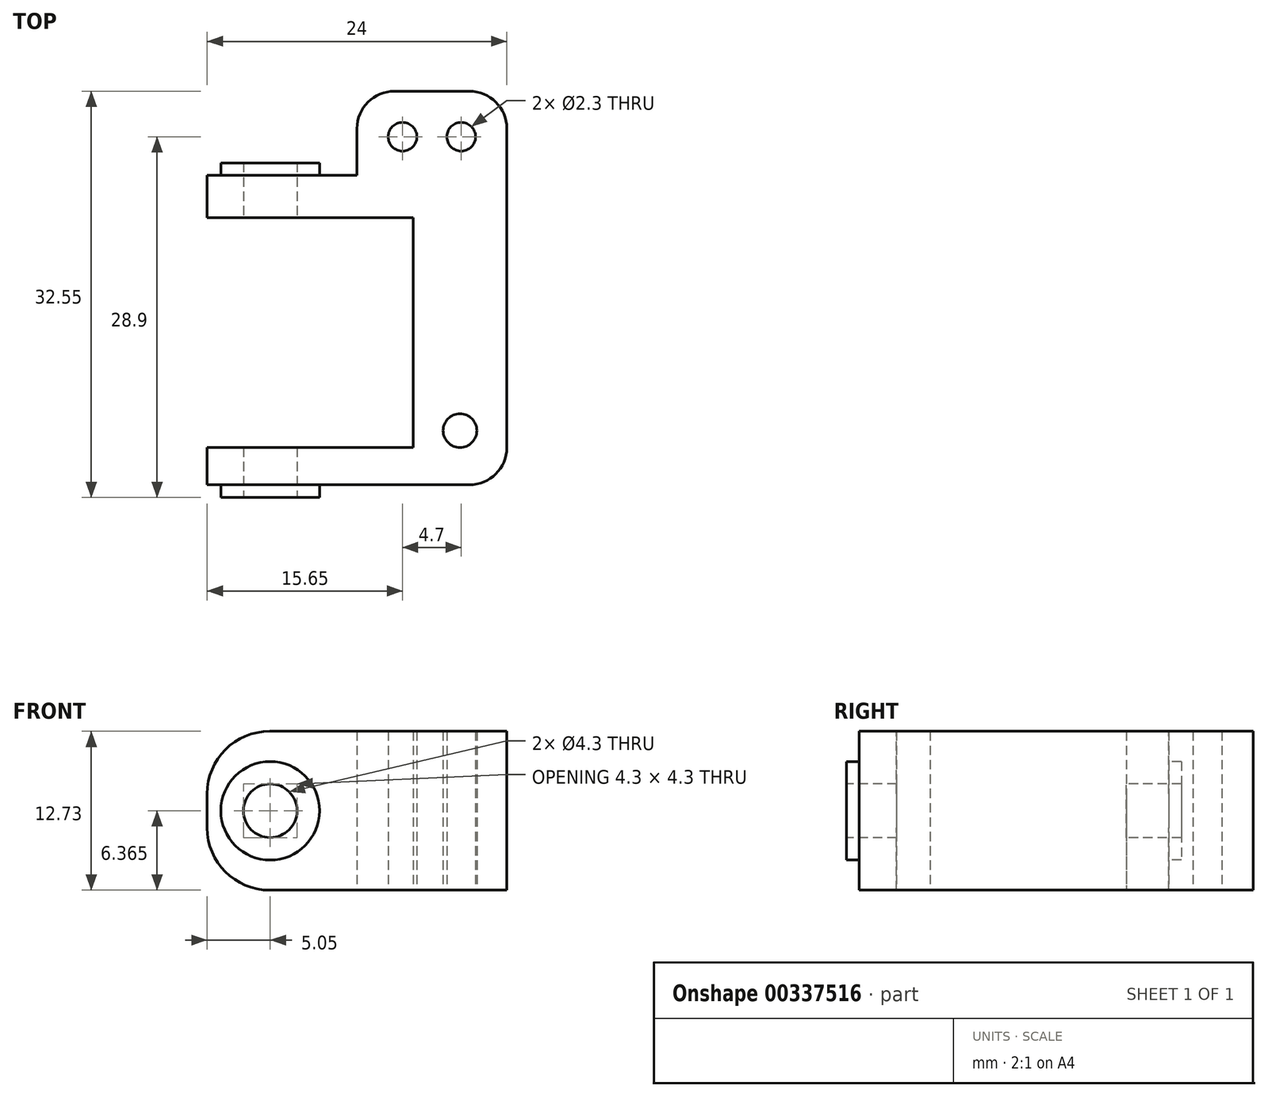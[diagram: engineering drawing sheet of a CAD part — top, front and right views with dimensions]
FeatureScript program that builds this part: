
annotation { "Feature Type Name" : "Feature", "Feature Type Description" : "" }
export const myFeature = defineFeature(function(context is Context, id is Id, definition is map)
    precondition{}
    {
        {
            var Q0;
            Q0=qCreatedBy(makeId("Top.planeOp"),FACE);
            var sketch = newSketch(context, id + "F0", { "sketchPlane" : qUnion([Q0])});
            skCircle(sketch, "E0", {"center": v(0, 0) * mm, "radius": 1.35 * mm});
            skLineSegment(sketch, "E1", {"start": v(1.35, 0) * mm, "end": v(3.75, 0) * mm, "construction": true});
            skLineSegment(sketch, "E2", {"start": v(3.75, 0) * mm, "end": v(3.75, -4.35) * mm});
            skLineSegment(sketch, "E3", {"start": v(3.75, -4.35) * mm, "end": v(-20.25, -4.35) * mm});
            skLineSegment(sketch, "E4", {"start": v(-20.25, -4.35) * mm, "end": v(-20.25, -1.35) * mm});
            skLineSegment(sketch, "E5", {"start": v(0, -1.35) * mm, "end": v(0, -4.35) * mm, "construction": true});
            skLineSegment(sketch, "E6", {"start": v(3.75, 0) * mm, "end": v(3.75, 27.2) * mm});
            skLineSegment(sketch, "E7", {"start": v(-20.25, -1.35) * mm, "end": v(-3.75, -1.35) * mm});
            skLineSegment(sketch, "E8", {"start": v(-3.75, -1.35) * mm, "end": v(-3.75, 17.05) * mm});
            skLineSegment(sketch, "E9", {"start": v(-1.35, 0) * mm, "end": v(-3.75, 0) * mm, "construction": true});
            skLineSegment(sketch, "E10", {"start": v(0, 1.35) * mm, "end": v(0, 4.35) * mm, "construction": true});
            skLineSegment(sketch, "E11", {"start": v(0, 4.35) * mm, "end": v(3.75, 4.35) * mm, "construction": true});
            skLineSegment(sketch, "E12", {"start": v(0, 4.35) * mm, "end": v(-3.75, 4.35) * mm, "construction": true});
            skLineSegment(sketch, "E13", {"start": v(3.75, 27.2) * mm, "end": v(-8.25, 27.2) * mm});
            skLineSegment(sketch, "E14", {"start": v(-8.25, 27.2) * mm, "end": v(-8.25, 20.45) * mm});
            skLineSegment(sketch, "E15", {"start": v(-8.25, 20.45) * mm, "end": v(3.75, 20.45) * mm, "construction": true});
            skLineSegment(sketch, "E16", {"start": v(-3.75, 17.05) * mm, "end": v(-3.75, 20.45) * mm});
            skLineSegment(sketch, "E17", {"start": v(-3.75, 17.05) * mm, "end": v(-20.25, 17.05) * mm});
            skLineSegment(sketch, "E18", {"start": v(-20.25, 17.05) * mm, "end": v(-20.25, 20.45) * mm});
            skLineSegment(sketch, "E19", {"start": v(-20.25, 20.45) * mm, "end": v(-8.25, 20.45) * mm});
            skCircle(sketch, "E20", {"center": v(0.1, 23.55) * mm, "radius": 1.15 * mm});
            skLineSegment(sketch, "E21", {"start": v(1.25, 23.55) * mm, "end": v(3.75, 23.55) * mm, "construction": true});
            skLineSegment(sketch, "E22", {"start": v(0.1, 24.7) * mm, "end": v(0.1, 27.2) * mm, "construction": true});
            skLineSegment(sketch, "E23", {"start": v(0.1, 23.55) * mm, "end": v(1.25, 23.55) * mm, "construction": true});
            skLineSegment(sketch, "E24", {"start": v(0.1, 23.55) * mm, "end": v(0.1, 24.7) * mm, "construction": true});
            skCircle(sketch, "E25", {"center": v(-4.6, 23.55) * mm, "radius": 1.15 * mm});
            skLineSegment(sketch, "E26", {"start": v(-4.6, 24.7) * mm, "end": v(-4.6, 27.2) * mm, "construction": true});
            skLineSegment(sketch, "E27", {"start": v(-5.75, 23.55) * mm, "end": v(-8.25, 23.55) * mm, "construction": true});
            skLineSegment(sketch, "E28", {"start": v(-4.6, 23.55) * mm, "end": v(-5.75, 23.55) * mm, "construction": true});
            skLineSegment(sketch, "E29", {"start": v(-4.6, 24.7) * mm, "end": v(-4.6, 23.55) * mm, "construction": true});
            skSolve(sketch);
        }
        {
            var Q0;
            Q0=makeQuery(id+"F0.imprint","IMPRINT",FACE,{"disambiguationData":[TD([[makeQuery(id+"F0.imprint","IMPRINT",EDGE,{"derivedFrom":sQuery(id+"F0.wireOp",EDGE,"E0")}),-1.0]])]});
            extrude(context, id + "F1", {"entities" : qUnion([Q0]), "depth" : 12.73 * mm});
        }
        {
            var Q0;
            Q0=makeQuery(id+"F1.opExtrude","SWEPT_FACE",FACE,{"disambiguationData":[OSD([sQuery(id+"F0.wireOp",EDGE,"E3")])]});
            var sketch = newSketch(context, id + "F2", { "sketchPlane" : qUnion([Q0])});
            skCircle(sketch, "E30", {"center": v(-15.2, 6.37) * mm, "radius": 2.15 * mm});
            skPoint(sketch, "E30.centerSnap0", {"position": v(-20.25, 6.37) * mm});
            skLineSegment(sketch, "E31", {"start": v(-20.25, 6.37) * mm, "end": v(-17.35, 6.37) * mm});
            skCircle(sketch, "E32", {"center": v(-15.2, 6.37) * mm, "radius": 3.95 * mm});
            skSolve(sketch);
        }
        {
            var Q0;
            Q0=makeQuery(id+"F2.imprint","IMPRINT",FACE,{"disambiguationData":[TD([[makeQuery(id+"F2.imprint","IMPRINT",EDGE,{"derivedFrom":sQuery(id+"F2.wireOp",EDGE,"E30")}),1.0]])]});
            extrude(context, id + "F3", {"entities" : qUnion([Q0]), "operationType" : NewBodyOperationType.REMOVE, "oppositeDirection" : true, "depth" : 25 * mm});
        }
        {
            var Q0;
            Q0=makeQuery(id+"F1.opExtrude","CAP_EDGE",EDGE,{"disambiguationData":[OSD([sQuery(id+"F0.wireOp",EDGE,"E4")])],"isStart":false});
            var Q1;
            Q1=makeQuery(id+"F1.opExtrude","CAP_EDGE",EDGE,{"disambiguationData":[OSD([sQuery(id+"F0.wireOp",EDGE,"E18")])],"isStart":false});
            var Q2;
            Q2=makeQuery(id+"F1.opExtrude","CAP_EDGE",EDGE,{"disambiguationData":[OSD([sQuery(id+"F0.wireOp",EDGE,"E4")])],"isStart":true});
            var Q3;
            Q3=makeQuery(id+"F1.opExtrude","CAP_EDGE",EDGE,{"disambiguationData":[OSD([sQuery(id+"F0.wireOp",EDGE,"E18")])],"isStart":true});
            fillet(context, id + "F4", {"entities" : qUnion([Q0, Q1, Q2, Q3]), "radius" : 5 * mm, "tangentPropagation" : true, "allowEdgeOverflow" : false});
        }
        {
            var Q0;
            Q0=makeQuery(id+"F1.opExtrude","SWEPT_EDGE",EDGE,{"disambiguationData":[OSD([sQuery(id+"F0.wireOp",EDGE,"E2"),sQuery(id+"F0.wireOp",EDGE,"E3")])]});
            fillet(context, id + "F5", {"entities" : qUnion([Q0]), "radius" : 3 * mm, "tangentPropagation" : true, "allowEdgeOverflow" : false});
        }
        {
            var Q0;
            Q0=makeQuery(id+"F1.opExtrude","SWEPT_EDGE",EDGE,{"disambiguationData":[OSD([sQuery(id+"F0.wireOp",EDGE,"E13"),sQuery(id+"F0.wireOp",EDGE,"E14")])]});
            var Q1;
            Q1=makeQuery(id+"F1.opExtrude","SWEPT_EDGE",EDGE,{"disambiguationData":[OSD([sQuery(id+"F0.wireOp",EDGE,"E6"),sQuery(id+"F0.wireOp",EDGE,"E13")])]});
            fillet(context, id + "F6", {"entities" : qUnion([Q0, Q1]), "radius" : 3 * mm, "tangentPropagation" : true, "allowEdgeOverflow" : false});
        }
        {
            var Q0;
            Q0=makeQuery(id+"F2.imprint","IMPRINT",FACE,{"disambiguationData":[TD([[makeQuery(id+"F2.imprint","IMPRINT",EDGE,{"derivedFrom":sQuery(id+"F2.wireOp",EDGE,"E30")}),-1.0]])]});
            extrude(context, id + "F7", {"entities" : qUnion([Q0]), "operationType" : NewBodyOperationType.ADD, "depth" : 1 * mm});
        }
        {
            var Q0;
            Q0=makeQuery(id+"F1.opExtrude","SWEPT_FACE",FACE,{"disambiguationData":[OSD([sQuery(id+"F0.wireOp",EDGE,"E19")])]});
            var sketch = newSketch(context, id + "F8", { "sketchPlane" : qUnion([Q0])});
            skLineSegment(sketch, "E33", {"start": v(20.25, 6.37) * mm, "end": v(13.05, 6.37) * mm});
            skCircle(sketch, "E34", {"center": v(15.2, 6.37) * mm, "radius": 2.1 * mm});
            skCircle(sketch, "E35", {"center": v(15.2, 6.37) * mm, "radius": 3.95 * mm});
            skSolve(sketch);
        }
        {
            var Q0;
            Q0=makeQuery(id+"F8.imprint","IMPRINT",FACE,{"disambiguationData":[TD([[makeQuery(id+"F8.imprint","IMPRINT",EDGE,{"derivedFrom":sQuery(id+"F8.wireOp",EDGE,"E35")}),1.0]])]});
            extrude(context, id + "F9", {"entities" : qUnion([Q0]), "operationType" : NewBodyOperationType.ADD, "depth" : 1 * mm});
        }
    });
